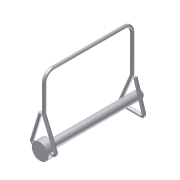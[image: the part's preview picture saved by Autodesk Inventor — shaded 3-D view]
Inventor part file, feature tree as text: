
AUTODESK INVENTOR PART (.ipt)
format: ipt  version: 2012 (Build 160160000, 160)  size: 170,496 bytes
history: native  units: in
note: dims shown in document units (in); Inventor stores cm internally (conversion verified against a paired STEP export)
features: sketch x6, plane x4, extrude x2, fillet x1, chamfer x1, sweep x1, other x1, projected_geometry x1
ambient origin geometry x8: Origin, YZ Plane, XZ Plane, XY Plane, X Axis, Y Axis, Z Axis, Center Point
bodies: Solid1 (feature_tree)
feature tree (17):
  sketch  "Sketch1"  dims[d6=0.495in d8=0.25in d9=0.0in d10=0.01in]
  extrude  "Extrusion1"  Depth=0.25in TaperAngle=0.0deg
  fillet  "Fillet1"  Radius=0.01in
  extrude  "Extrusion2"  Depth=2.75in TaperAngle=0.0deg
  chamfer  "Chamfer1"  Distance=0.025in Angle=45.0deg
  plane  "Work Plane1"
  sketch  "Sketch2"  dims[d11=0.245in d12=2.75in d13=0.0in d14=0.025in d15=0.125in d16=45.0deg]
  plane  "Work Plane2"
  sketch  "Sketch3"  dims[d17=0.0in d18=0.125in]
  sketch  "Sketch4"  dims[d19=0.095in]
  plane  "Work Plane3"
  sketch  "Sketch5"  dims[d20=-0.125in]
  plane  "Work Plane4"
  sweep  "Sweep1"
  other  "Work Axis1"
  projected_geometry  "Projected Loop1"
  sketch  "Sketch6"  dims[d21=0.75in d22=0.9in d23=0.9in d24=0.375in d25=0.1in d26=0.06in d27=1.715in d28=0.25in d29=0.25in d31=0.25in d32=2.625in d33=2.015in d34=0.75in d35=0.375in d36=0.1in d37=0.9in d38=0.9in d39=0.06in d40=0.06in d41=0.095in d42=0.0in]
